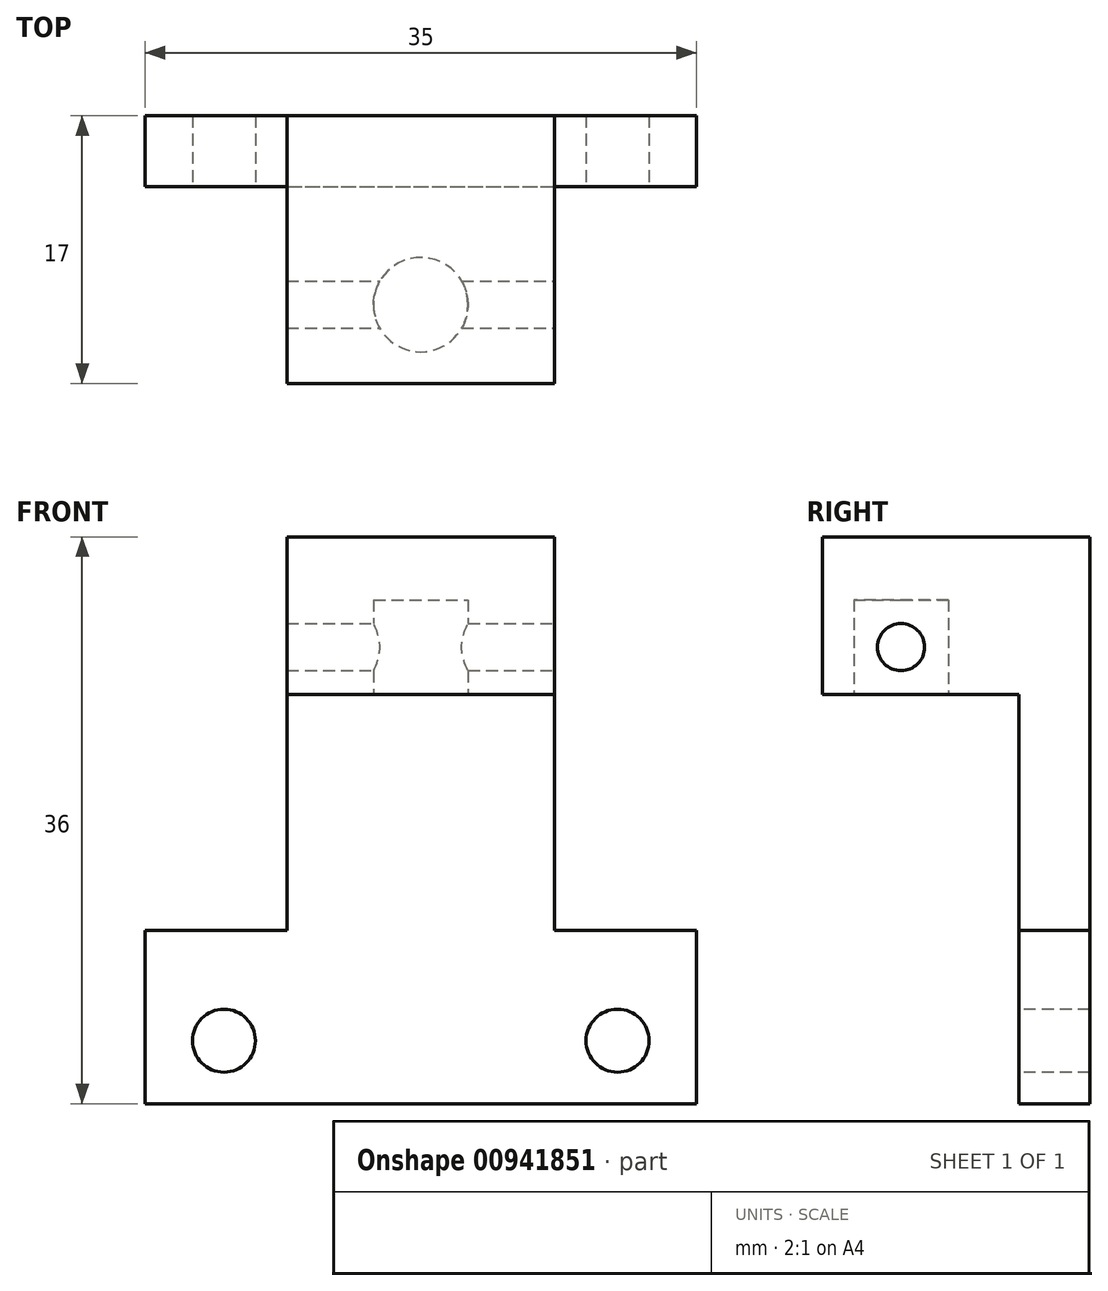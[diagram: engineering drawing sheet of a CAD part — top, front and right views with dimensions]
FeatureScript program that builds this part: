
annotation { "Feature Type Name" : "Feature", "Feature Type Description" : "" }
export const myFeature = defineFeature(function(context is Context, id is Id, definition is map)
    precondition{}
    {
        {
            var Q0;
            Q0=qCreatedBy(makeId("Front.planeOp"),FACE);
            var sketch = newSketch(context, id + "F0", { "sketchPlane" : qUnion([Q0])});
            skLineSegment(sketch, "E0.bottom", {"start": v(-17.5, 25) * mm, "end": v(17.5, 25) * mm});
            skLineSegment(sketch, "E0.top", {"start": v(-17.5, -20) * mm, "end": v(17.5, -20) * mm});
            skLineSegment(sketch, "E0.left", {"start": v(-17.5, 25) * mm, "end": v(-17.5, -20) * mm});
            skLineSegment(sketch, "E0.right", {"start": v(17.5, 25) * mm, "end": v(17.5, -20) * mm});
            skPoint(sketch, "E0.middle", {"position": v(0, 2.5) * mm});
            skSolve(sketch);
        }
        {
            var Q0;
            Q0=makeQuery(id+"F0.imprint","IMPRINT",FACE,{"disambiguationData":[TD([[makeQuery(id+"F0.imprint","IMPRINT",EDGE,{"derivedFrom":sQuery(id+"F0.wireOp",EDGE,"E0.bottom")}),-1.0]])]});
            extrude(context, id + "F1", {"entities" : qUnion([Q0]), "depth" : 4.5 * mm, "offsetDistance" : 25 * mm});
        }
        {
            var Q0;
            Q0=makeQuery(id+"F1.opExtrude","CAP_FACE",FACE,{"disambiguationData":[OSD([sQuery(id+"F0.wireOp",EDGE,"E0.bottom"),sQuery(id+"F0.wireOp",EDGE,"E0.top"),sQuery(id+"F0.wireOp",EDGE,"E0.left"),sQuery(id+"F0.wireOp",EDGE,"E0.right")])],"isStart":false});
            var sketch = newSketch(context, id + "F2", { "sketchPlane" : qUnion([Q0])});
            skCircle(sketch, "E1", {"center": v(12.5, -15) * mm, "radius": 2 * mm});
            skCircle(sketch, "E2.MirrorC", {"center": v(-12.5, -15) * mm, "radius": 2 * mm});
            skCircle(sketch, "E3.MirrorC", {"center": v(-12.5, -7) * mm, "radius": 2 * mm});
            skCircle(sketch, "E4.MirrorC", {"center": v(12.5, -7) * mm, "radius": 2 * mm});
            skSolve(sketch);
        }
        {
            var Q0;
            Q0=qSketchRegion(id+"F2",true);
            extrude(context, id + "F3", {"entities" : qUnion([Q0]), "operationType" : NewBodyOperationType.REMOVE, "oppositeDirection" : true, "depth" : 10 * mm, "offsetDistance" : 25 * mm});
        }
        {
            var Q0;
            Q0=makeQuery(id+"F1.opExtrude","CAP_FACE",FACE,{"disambiguationData":[OSD([sQuery(id+"F0.wireOp",EDGE,"E0.bottom"),sQuery(id+"F0.wireOp",EDGE,"E0.top"),sQuery(id+"F0.wireOp",EDGE,"E0.left"),sQuery(id+"F0.wireOp",EDGE,"E0.right")])],"isStart":false});
            var sketch = newSketch(context, id + "F4", { "sketchPlane" : qUnion([Q0])});
            skLineSegment(sketch, "E5.bottom", {"start": v(-17.5, 25) * mm, "end": v(17.5, 25) * mm});
            skLineSegment(sketch, "E5.top", {"start": v(-17.5, 15) * mm, "end": v(17.5, 15) * mm});
            skLineSegment(sketch, "E5.left", {"start": v(-17.5, 25) * mm, "end": v(-17.5, 15) * mm});
            skLineSegment(sketch, "E5.right", {"start": v(17.5, 25) * mm, "end": v(17.5, 15) * mm});
            skSolve(sketch);
        }
        {
            var Q0;
            Q0=qSketchRegion(id+"F4",true);
            extrude(context, id + "F5", {"entities" : qUnion([Q0]), "operationType" : NewBodyOperationType.ADD, "depth" : 12.5 * mm, "offsetDistance" : 25 * mm});
        }
        {
            var Q0;
            Q0=makeQuery(id+"F5.opExtrude","SWEPT_FACE",FACE,{"disambiguationData":[OSD([sQuery(id+"F4.wireOp",EDGE,"E5.top")])]});
            var sketch = newSketch(context, id + "F6", { "sketchPlane" : qUnion([Q0])});
            skCircle(sketch, "E6", {"center": v(0, 12) * mm, "radius": 3 * mm});
            skPoint(sketch, "E6.centerSnap0", {"position": v(17.5, 12) * mm});
            skPoint(sketch, "E6.centerSnap1", {"position": v(0, 17) * mm});
            skSolve(sketch);
        }
        {
            var Q0;
            Q0=qSketchRegion(id+"F6",true);
            extrude(context, id + "F7", {"entities" : qUnion([Q0]), "operationType" : NewBodyOperationType.REMOVE, "oppositeDirection" : true, "depth" : 6 * mm, "offsetDistance" : 25 * mm});
        }
        {
            var Q0;
            Q0=makeQuery(id+"F1.opExtrude","SWEPT_FACE",FACE,{"disambiguationData":[OSD([sQuery(id+"F0.wireOp",EDGE,"E0.top")])]});
            var sketch = newSketch(context, id + "F8", { "sketchPlane" : qUnion([Q0])});
            skLineSegment(sketch, "E7.0.0", {"start": v(-17.5, 0) * mm, "end": v(17.5, 0) * mm});
            skLineSegment(sketch, "E7.0.1", {"start": v(17.5, 0) * mm, "end": v(17.5, 4.5) * mm});
            skLineSegment(sketch, "E7.0.2", {"start": v(17.5, 4.5) * mm, "end": v(-17.5, 4.5) * mm});
            skLineSegment(sketch, "E7.0.3", {"start": v(-17.5, 4.5) * mm, "end": v(-17.5, 0) * mm});
            skSolve(sketch);
        }
        {
            var Q0;
            Q0=qSketchRegion(id+"F8",true);
            extrude(context, id + "F9", {"entities" : qUnion([Q0]), "operationType" : NewBodyOperationType.REMOVE, "oppositeDirection" : true, "depth" : 2 * mm, "offsetDistance" : 25 * mm});
        }
        {
            var Q0;
            Q0=makeQuery(id+"F5.opExtrude","CAP_FACE",FACE,{"disambiguationData":[OSD([sQuery(id+"F4.wireOp",EDGE,"E5.bottom"),sQuery(id+"F4.wireOp",EDGE,"E5.top"),sQuery(id+"F4.wireOp",EDGE,"E5.left"),sQuery(id+"F4.wireOp",EDGE,"E5.right")])],"isStart":false});
            var sketch = newSketch(context, id + "F10", { "sketchPlane" : qUnion([Q0])});
            skLineSegment(sketch, "E8.bottom", {"start": v(-17.5, 25) * mm, "end": v(-8.5, 25) * mm});
            skLineSegment(sketch, "E8.top", {"start": v(-17.5, 0) * mm, "end": v(-8.5, 0) * mm});
            skLineSegment(sketch, "E8.left", {"start": v(-17.5, 25) * mm, "end": v(-17.5, 0) * mm});
            skLineSegment(sketch, "E8.right", {"start": v(-8.5, 25) * mm, "end": v(-8.5, 0) * mm});
            skLineSegment(sketch, "E9.MirrorCS", {"start": v(17.5, 25) * mm, "end": v(8.5, 25) * mm});
            skLineSegment(sketch, "E10.MirrorCS", {"start": v(8.5, 25) * mm, "end": v(8.5, 0) * mm});
            skLineSegment(sketch, "E11.MirrorCS", {"start": v(17.5, 0) * mm, "end": v(8.5, 0) * mm});
            skLineSegment(sketch, "E12.MirrorCS", {"start": v(17.5, 25) * mm, "end": v(17.5, 0) * mm});
            skSolve(sketch);
        }
        {
            var Q0;
            Q0=qSketchRegion(id+"F10",true);
            extrude(context, id + "F11", {"entities" : qUnion([Q0]), "operationType" : NewBodyOperationType.REMOVE, "endBound" : BoundingType.THROUGH_ALL, "oppositeDirection" : true, "depth" : 25 * mm, "offsetDistance" : 25 * mm});
        }
        {
            var Q0;
            Q0=makeQuery(id+"F11.boolean.opBoolean","COPY",FACE,{"derivedFrom":makeQuery(id+"F11.opExtrude","SWEPT_FACE",FACE,{"disambiguationData":[OSD([sQuery(id+"F10.wireOp",EDGE,"E10.MirrorCS")])]})});
            var sketch = newSketch(context, id + "F12", { "sketchPlane" : qUnion([Q0])});
            skCircle(sketch, "E13", {"center": v(-12, 18) * mm, "radius": 1.5 * mm});
            skSolve(sketch);
        }
        {
            var Q0;
            Q0=qSketchRegion(id+"F12",true);
            extrude(context, id + "F13", {"entities" : qUnion([Q0]), "operationType" : NewBodyOperationType.REMOVE, "endBound" : BoundingType.THROUGH_ALL, "oppositeDirection" : true, "depth" : 25 * mm, "offsetDistance" : 25 * mm});
        }
        {
            var Q0;
            Q0=makeQuery(id+"F1.opExtrude","CAP_FACE",FACE,{"disambiguationData":[OSD([sQuery(id+"F0.wireOp",EDGE,"E0.bottom"),sQuery(id+"F0.wireOp",EDGE,"E0.top"),sQuery(id+"F0.wireOp",EDGE,"E0.left"),sQuery(id+"F0.wireOp",EDGE,"E0.right")])],"isStart":false});
            var sketch = newSketch(context, id + "F14", { "sketchPlane" : qUnion([Q0])});
            skLineSegment(sketch, "E14.bottom", {"start": v(-17.5, -18) * mm, "end": v(17.5, -18) * mm});
            skLineSegment(sketch, "E14.top", {"start": v(-17.5, -12) * mm, "end": v(17.5, -12) * mm});
            skLineSegment(sketch, "E14.left", {"start": v(-17.5, -18) * mm, "end": v(-17.5, -12) * mm});
            skLineSegment(sketch, "E14.right", {"start": v(17.5, -18) * mm, "end": v(17.5, -12) * mm});
            skSolve(sketch);
        }
        {
            var Q0;
            Q0=qSketchRegion(id+"F14",true);
            extrude(context, id + "F15", {"entities" : qUnion([Q0]), "operationType" : NewBodyOperationType.REMOVE, "endBound" : BoundingType.THROUGH_ALL, "oppositeDirection" : true, "depth" : 25 * mm, "offsetDistance" : 25 * mm});
        }
        {
            var Q0;
            Q0=makeQuery(id+"F15.boolean.opBoolean","COPY",FACE,{"derivedFrom":makeQuery(id+"F15.opExtrude","SWEPT_FACE",FACE,{"disambiguationData":[OSD([sQuery(id+"F14.wireOp",EDGE,"E14.top")])]})});
            var sketch = newSketch(context, id + "F16", { "sketchPlane" : qUnion([Q0])});
            skLineSegment(sketch, "E15.0.0", {"start": v(-17.5, 0) * mm, "end": v(17.5, 0) * mm});
            skLineSegment(sketch, "E15.0.1", {"start": v(17.5, 0) * mm, "end": v(17.5, 4.5) * mm});
            skLineSegment(sketch, "E15.0.2", {"start": v(17.5, 4.5) * mm, "end": v(-17.5, 4.5) * mm});
            skLineSegment(sketch, "E15.0.3", {"start": v(-17.5, 4.5) * mm, "end": v(-17.5, 0) * mm});
            skSolve(sketch);
        }
        {
            var Q0;
            Q0=qSketchRegion(id+"F16",true);
            extrude(context, id + "F17", {"entities" : qUnion([Q0]), "operationType" : NewBodyOperationType.REMOVE, "oppositeDirection" : true, "depth" : 1 * mm, "offsetDistance" : 25 * mm});
        }
    });
